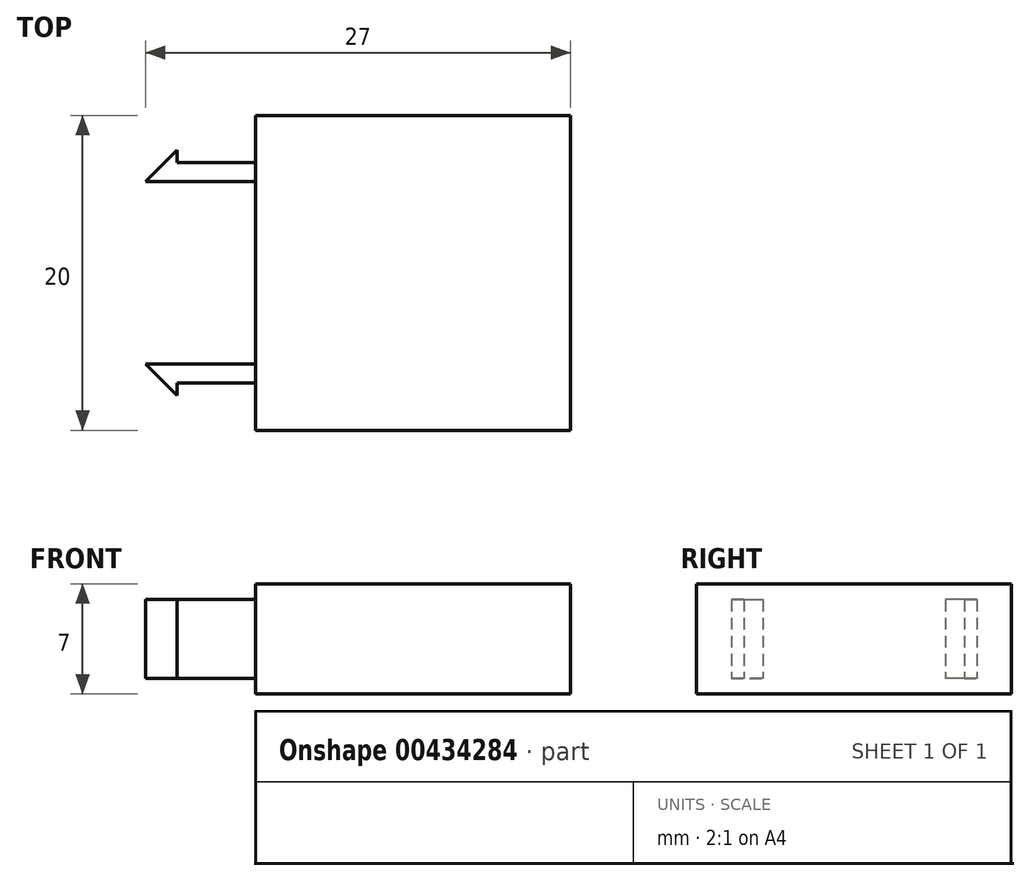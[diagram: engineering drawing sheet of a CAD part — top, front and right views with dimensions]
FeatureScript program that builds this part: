
annotation { "Feature Type Name" : "Feature", "Feature Type Description" : "" }
export const myFeature = defineFeature(function(context is Context, id is Id, definition is map)
    precondition{}
    {
        {
            var Q0;
            Q0=qCreatedBy(makeId("Top.planeOp"),FACE);
            var sketch = newSketch(context, id + "F0", { "sketchPlane" : qUnion([Q0])});
            skLineSegment(sketch, "E0.bottom", {"start": v(10, 10) * mm, "end": v(-10, 10) * mm});
            skLineSegment(sketch, "E0.top", {"start": v(10, -10) * mm, "end": v(-10, -10) * mm});
            skLineSegment(sketch, "E0.left", {"start": v(10, 10) * mm, "end": v(10, -10) * mm});
            skLineSegment(sketch, "E0.right", {"start": v(-10, 10) * mm, "end": v(-10, -10) * mm});
            skPoint(sketch, "E0.middle", {"position": v(0, 0) * mm});
            skLineSegment(sketch, "E1.bottom", {"start": v(-10, 7) * mm, "end": v(-15, 7) * mm});
            skLineSegment(sketch, "E1.top", {"start": v(-10, 5.8) * mm, "end": v(-15, 5.8) * mm});
            skLineSegment(sketch, "E1.left", {"start": v(-10, 7) * mm, "end": v(-10, 5.8) * mm});
            skLineSegment(sketch, "E1.right", {"start": v(-15, 7) * mm, "end": v(-15, 5.8) * mm});
            skLineSegment(sketch, "E2", {"start": v(-15, 5.8) * mm, "end": v(-15, 7.8) * mm});
            skLineSegment(sketch, "E3", {"start": v(-15, 7.8) * mm, "end": v(-17, 5.8) * mm});
            skLineSegment(sketch, "E4", {"start": v(-17, 5.8) * mm, "end": v(-15, 5.8) * mm});
            skSolve(sketch);
        }
        {
            var Q0;
            {var subQ3=sQuery(id+"F0.wireOp",EDGE,"E3");Q0=makeQuery(id+"F0.imprint","IMPRINT",FACE,{"disambiguationData":[TD([[makeQuery(id+"F0.imprint","IMPRINT",EDGE,{"derivedFrom":subQ3}),1.0]])]});}
            var Q1;
            {var subQ0=sQuery(id+"F0.wireOp",EDGE,"E1.bottom");Q1=makeQuery(id+"F0.imprint","IMPRINT",FACE,{"disambiguationData":[TD([[makeQuery(id+"F0.imprint","IMPRINT",EDGE,{"derivedFrom":subQ0}),1.0]])]});}
            extrude(context, id + "F1", {"entities" : qUnion([Q0, Q1]), "depth" : 5 * mm});
        }
        {
            var Q0;
            {var subQ1=sQuery(id+"F0.wireOp",EDGE,"E0.bottom");Q0=makeQuery(id+"F0.imprint","IMPRINT",FACE,{"disambiguationData":[TD([[makeQuery(id+"F0.imprint","IMPRINT",EDGE,{"derivedFrom":subQ1}),1.0]])]});}
            extrude(context, id + "F2", {"entities" : qUnion([Q0]), "oppositeDirection" : true, "depth" : 1 * mm});
        }
        {
            var Q0;
            Q0=makeQuery(id+"F2.opExtrude","CAP_FACE",FACE,{"disambiguationData":[OSD([sQuery(id+"F0.wireOp",EDGE,"E0.bottom"),sQuery(id+"F0.wireOp",EDGE,"E0.top"),sQuery(id+"F0.wireOp",EDGE,"E0.left"),sQuery(id+"F0.wireOp",EDGE,"E0.right"),sQuery(id+"F0.wireOp",EDGE,"E1.left")])],"isStart":true});
            extrude(context, id + "F3", {"entities" : qUnion([Q0]), "depth" : 6 * mm});
        }
        {
            var Q0;
            Q0=makeQuery(id+"F1.opExtrude","SWEPT_BODY",BODY,{"disambiguationData":[OSD([sQuery(id+"F0.wireOp",EDGE,"E1.bottom"),sQuery(id+"F0.wireOp",EDGE,"E1.top"),sQuery(id+"F0.wireOp",EDGE,"E1.left"),sQuery(id+"F0.wireOp",EDGE,"E1.right"),sQuery(id+"F0.wireOp",EDGE,"4SCldlpt-8VIW-SOBm-z9p0-wjdZ3BOWXpox"),sQuery(id+"F0.wireOp",EDGE,"KFwTBkE5-UgRC-Or8S-yJCR-UznN1bh9Lncs")])]});
            var Q1;
            Q1=qCreatedBy(makeId("Front.planeOp"),FACE);
            mirror(context, id + "F4", {"operationType" : NewBodyOperationType.ADD, "entities" : qUnion([Q0]), "mirrorPlane" : qUnion([Q1])});
        }
    });
